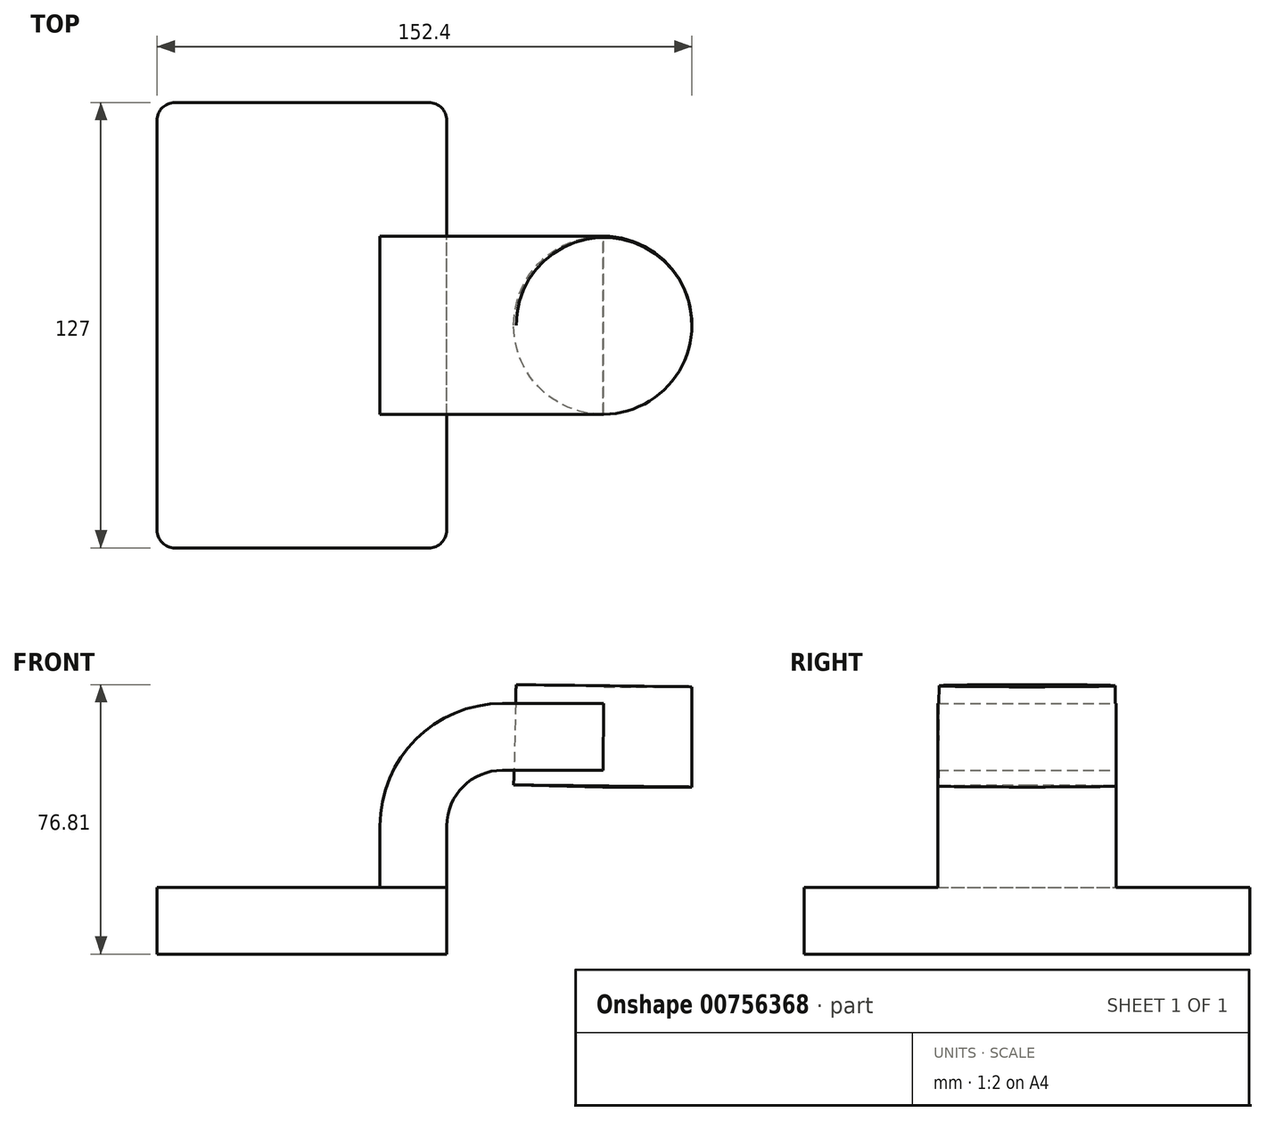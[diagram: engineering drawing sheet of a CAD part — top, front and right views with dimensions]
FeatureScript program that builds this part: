
annotation { "Feature Type Name" : "Feature", "Feature Type Description" : "" }
export const myFeature = defineFeature(function(context is Context, id is Id, definition is map)
    precondition{}
    {
        {
            var Q0;
            Q0=qCreatedBy(makeId("Front.planeOp"),FACE);
            var sketch = newSketch(context, id + "F0", { "sketchPlane" : qUnion([Q0])});
            skLineSegment(sketch, "E0.bottom", {"start": v(-41.28, -9.53) * mm, "end": v(41.28, -9.53) * mm});
            skLineSegment(sketch, "E0.top", {"start": v(-41.28, 9.53) * mm, "end": v(41.28, 9.53) * mm});
            skLineSegment(sketch, "E0.left", {"start": v(-41.28, -9.53) * mm, "end": v(-41.28, 9.53) * mm});
            skLineSegment(sketch, "E0.right", {"start": v(41.28, -9.53) * mm, "end": v(41.28, 9.53) * mm});
            skPoint(sketch, "E0.middle", {"position": v(0, 0) * mm});
            skLineSegment(sketch, "E1.bottom", {"start": v(60.32, 66.67) * mm, "end": v(111.12, 66.67) * mm});
            skLineSegment(sketch, "E1.top", {"start": v(60.32, 38.1) * mm, "end": v(111.12, 38.1) * mm});
            skLineSegment(sketch, "E1.left", {"start": v(60.32, 66.68) * mm, "end": v(60.32, 38.1) * mm});
            skLineSegment(sketch, "E1.right", {"start": v(111.12, 66.67) * mm, "end": v(111.12, 38.1) * mm});
            skPoint(sketch, "E1.middle", {"position": v(85.72, 52.39) * mm});
            skLineSegment(sketch, "E2", {"start": v(41.28, 9.52) * mm, "end": v(41.28, 27) * mm});
            skArc(sketch, "E3", {"start": v(41.27, 27) * mm, "mid": v(45.92, 38.23) * mm, "end": v(57.15, 42.88) * mm});
            skLineSegment(sketch, "E4", {"start": v(57.15, 42.88) * mm, "end": v(86.07, 42.88) * mm});
            skLineSegment(sketch, "E5.0", {"start": v(57.15, 61.93) * mm, "end": v(86.01, 61.93) * mm});
            skArc(sketch, "E5.1", {"start": v(22.22, 27) * mm, "mid": v(32.45, 51.7) * mm, "end": v(57.15, 61.93) * mm});
            skLineSegment(sketch, "E5.2", {"start": v(22.22, 9.52) * mm, "end": v(22.22, 27) * mm});
            skLineSegment(sketch, "E6", {"start": v(85.72, 38.1) * mm, "end": v(86.07, 66.67) * mm});
            skFitSpline(sketch, "E7", {"points": [v(-41.28, 9.53) * mm, v(57.15, 61.93) * mm], "startDerivative": vector(47.46, 111.2) * mm, "endDerivative": vector(144.29, -12.08) * mm});
            skSolve(sketch);
        }
        {
            var Q0;
            Q0=makeQuery(id+"F0.imprint","IMPRINT",FACE,{"disambiguationData":[TD([[makeQuery(id+"F0.imprint","IMPRINT",EDGE,{"derivedFrom":sQuery(id+"F0.wireOp",EDGE,"E0.bottom")}),1.0]])]});
            extrude(context, id + "F1", {"entities" : qUnion([Q0]), "endBound" : BoundingType.SYMMETRIC, "depth" : 127 * mm, "offsetDistance" : 25.4 * mm});
        }
        {
            var Q0;
            {var subQ1=sQuery(id+"F0.wireOp",EDGE,"E2");Q0=makeQuery(id+"F0.imprint","IMPRINT",FACE,{"disambiguationData":[TD([[makeQuery(id+"F0.imprint","IMPRINT",EDGE,{"derivedFrom":subQ1}),1.0]])]});}
            var Q1;
            {var subQ0=sQuery(id+"F0.wireOp",EDGE,"E5.0");var subQ1=sQuery(id+"F0.wireOp",EDGE,"E1.left");var subQ2=makeQuery(id+"F0.imprint","INTERSECT",VERTEX,{"derivedFrom":[subQ1,subQ0]});Q1=makeQuery(id+"F0.imprint","IMPRINT",FACE,{"disambiguationData":[TD([[makeQuery(id+"F0.imprint","IMPRINT",EDGE,{"disambiguationData":[TD([[subQ2,-1.0]])],"derivedFrom":subQ1}),1.0]])]});}
            extrude(context, id + "F2", {"entities" : qUnion([Q0, Q1]), "operationType" : NewBodyOperationType.ADD, "endBound" : BoundingType.SYMMETRIC, "depth" : 50.8 * mm, "offsetDistance" : 25.4 * mm});
        }
        {
            var Q0;
            Q0=makeQuery(id+"F0.imprint","IMPRINT",FACE,{"disambiguationData":[TD([[makeQuery(id+"F0.imprint","IMPRINT",EDGE,{"derivedFrom":sQuery(id+"F0.wireOp",EDGE,"E5.1")}),1.0]])]});
            extrude(context, id + "F3", {"entities" : qUnion([Q0]), "operationType" : NewBodyOperationType.ADD, "endBound" : BoundingType.SYMMETRIC, "depth" : 15.88 * mm, "offsetDistance" : 25.4 * mm});
        }
        {
            var Q0;
            Q0=makeQuery(id+"F1.opExtrude","CAP_EDGE",EDGE,{"disambiguationData":[OSD([sQuery(id+"F0.wireOp",EDGE,"E0.left")])],"isStart":false});
            var Q1;
            Q1=makeQuery(id+"F1.opExtrude","CAP_EDGE",EDGE,{"disambiguationData":[OSD([sQuery(id+"F0.wireOp",EDGE,"E0.right")])],"isStart":false});
            var Q2;
            Q2=makeQuery(id+"F1.opExtrude","CAP_EDGE",EDGE,{"disambiguationData":[OSD([sQuery(id+"F0.wireOp",EDGE,"E0.right")])],"isStart":true});
            var Q3;
            Q3=makeQuery(id+"F1.opExtrude","CAP_EDGE",EDGE,{"disambiguationData":[OSD([sQuery(id+"F0.wireOp",EDGE,"E0.left")])],"isStart":true});
            fillet(context, id + "F4", {"entities" : qUnion([Q0, Q1, Q2, Q3]), "radius" : 5.08 * mm, "tangentPropagation" : true, "allowEdgeOverflow" : false});
        }
        {
            var Q0;
            {var subQ0=sQuery(id+"F0.wireOp",EDGE,"E1.right");Q0=makeQuery(id+"F0.imprint","IMPRINT",FACE,{"disambiguationData":[TD([[makeQuery(id+"F0.imprint","IMPRINT",EDGE,{"derivedFrom":subQ0}),-1.0]])]});}
            var Q1;
            Q1=sQuery(id+"F0.wireOp",EDGE,"E6");
            revolve(context, id + "F5", {"surfaceOperationType" : NewSurfaceOperationType.NEW, "entities" : qUnion([Q0]), "axis" : qUnion([Q1]), "revolveType" : RevolveType.FULL});
        }
    });
